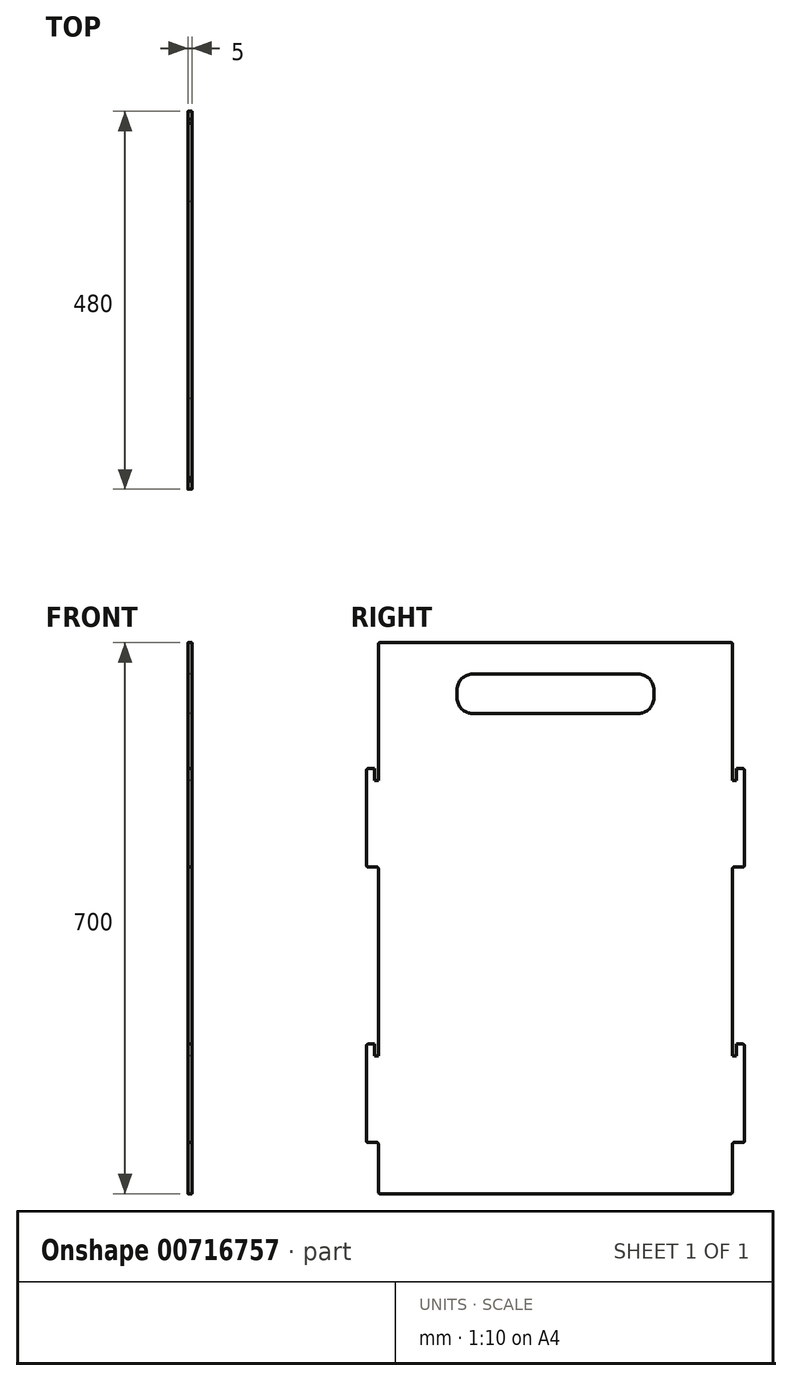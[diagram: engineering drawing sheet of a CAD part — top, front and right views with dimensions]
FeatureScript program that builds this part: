
annotation { "Feature Type Name" : "Feature", "Feature Type Description" : "" }
export const myFeature = defineFeature(function(context is Context, id is Id, definition is map)
    precondition{}
    {
        {
            var Q0;
            Q0=qCreatedBy(makeId("Right.planeOp"),FACE);
            var sketch = newSketch(context, id + "F0", { "sketchPlane" : qUnion([Q0])});
            skLineSegment(sketch, "E0.bottom", {"start": v(2, 0) * mm, "end": v(448, 0) * mm});
            skLineSegment(sketch, "E0.top", {"start": v(2, 700) * mm, "end": v(448, 700) * mm});
            skLineSegment(sketch, "E0.left", {"start": v(0, 2) * mm, "end": v(0, 63) * mm});
            skLineSegment(sketch, "E0.right", {"start": v(450, 2) * mm, "end": v(450, 63) * mm});
            skLineSegment(sketch, "E1.bottom", {"start": v(330, 610) * mm, "end": v(120, 610) * mm});
            skLineSegment(sketch, "E1.top", {"start": v(330, 660) * mm, "end": v(120, 660) * mm});
            skLineSegment(sketch, "E1.left", {"start": v(350, 630) * mm, "end": v(350, 640) * mm});
            skLineSegment(sketch, "E1.right", {"start": v(100, 630) * mm, "end": v(100, 640) * mm});
            skPoint(sketch, "E1.middle", {"position": v(225, 635) * mm});
            skPoint(sketch, "E2.visualSharp", {"position": v(100, 660) * mm});
            skArc(sketch, "E2.filletArc", {"start": v(120, 660) * mm, "mid": v(105.86, 654.14) * mm, "end": v(100, 640) * mm});
            skPoint(sketch, "E3.visualSharp", {"position": v(100, 610) * mm});
            skArc(sketch, "E3.filletArc", {"start": v(100, 630) * mm, "mid": v(105.86, 615.86) * mm, "end": v(120, 610) * mm});
            skPoint(sketch, "E4.visualSharp", {"position": v(350, 660) * mm});
            skArc(sketch, "E4.filletArc", {"start": v(350, 640) * mm, "mid": v(344.14, 654.14) * mm, "end": v(330, 660) * mm});
            skPoint(sketch, "E5.visualSharp", {"position": v(350, 610) * mm});
            skArc(sketch, "E5.filletArc", {"start": v(330, 610) * mm, "mid": v(344.14, 615.86) * mm, "end": v(350, 630) * mm});
            skLineSegment(sketch, "E6.bottom", {"start": v(-5, 540) * mm, "end": v(-13, 540) * mm});
            skLineSegment(sketch, "E6.top", {"start": v(-2, 415) * mm, "end": v(-13, 415) * mm});
            skLineSegment(sketch, "E6.right", {"start": v(-15, 538) * mm, "end": v(-15, 417) * mm});
            skLineSegment(sketch, "E7.bottom", {"start": v(-5, 190) * mm, "end": v(-13, 190) * mm});
            skLineSegment(sketch, "E7.top", {"start": v(-2, 65) * mm, "end": v(-13, 65) * mm});
            skLineSegment(sketch, "E7.right", {"start": v(-15, 188) * mm, "end": v(-15, 67) * mm});
            skLineSegment(sketch, "E8.trimOffspring", {"start": v(0, 525) * mm, "end": v(0, 698) * mm});
            skLineSegment(sketch, "E9.trimOffspring", {"start": v(0, 190) * mm, "end": v(0, 413) * mm});
            skLineSegment(sketch, "E10", {"start": v(225, 700) * mm, "end": v(225, 0) * mm, "construction": true});
            skLineSegment(sketch, "E11.MirrorCS", {"start": v(452, 65) * mm, "end": v(463, 65) * mm});
            skLineSegment(sketch, "E12.MirrorCS", {"start": v(465, 188) * mm, "end": v(465, 67) * mm});
            skLineSegment(sketch, "E13.MirrorCS", {"start": v(455, 190) * mm, "end": v(463, 190) * mm});
            skLineSegment(sketch, "E14.MirrorCS", {"start": v(452, 415) * mm, "end": v(463, 415) * mm});
            skLineSegment(sketch, "E15.MirrorCS", {"start": v(455, 540) * mm, "end": v(463, 540) * mm});
            skLineSegment(sketch, "E16.MirrorCS", {"start": v(465, 538) * mm, "end": v(465, 417) * mm});
            skLineSegment(sketch, "E17.trimOffspring", {"start": v(450, 540) * mm, "end": v(450, 698) * mm});
            skLineSegment(sketch, "E18.trimOffspring", {"start": v(450, 190) * mm, "end": v(450, 413) * mm});
            skLineSegment(sketch, "E19.top", {"start": v(-5, 525) * mm, "end": v(0, 525) * mm});
            skLineSegment(sketch, "E19.left", {"start": v(-5, 540) * mm, "end": v(-5, 525) * mm});
            skLineSegment(sketch, "E20.top", {"start": v(-5, 175) * mm, "end": v(0, 175) * mm});
            skLineSegment(sketch, "E20.left", {"start": v(-5, 190) * mm, "end": v(-5, 175) * mm});
            skLineSegment(sketch, "E20.right", {"start": v(0, 200) * mm, "end": v(0, 175) * mm});
            skLineSegment(sketch, "E21.MirrorCS", {"start": v(455, 525) * mm, "end": v(450, 525) * mm});
            skLineSegment(sketch, "E22.MirrorCS", {"start": v(455, 540) * mm, "end": v(455, 525) * mm});
            skLineSegment(sketch, "E23.MirrorCS", {"start": v(455, 190) * mm, "end": v(455, 175) * mm});
            skLineSegment(sketch, "E24.MirrorCS", {"start": v(455, 175) * mm, "end": v(450, 175) * mm});
            skLineSegment(sketch, "E25", {"start": v(450, 540) * mm, "end": v(450, 525) * mm});
            skLineSegment(sketch, "E26", {"start": v(450, 190) * mm, "end": v(450, 175) * mm});
            skPoint(sketch, "E27.orphan", {"position": v(0, 540) * mm});
            skPoint(sketch, "E28.visualSharp", {"position": v(0, 700) * mm});
            skArc(sketch, "E28.filletArc", {"start": v(2, 700) * mm, "mid": v(0.59, 699.41) * mm, "end": v(0, 698) * mm});
            skPoint(sketch, "E29.visualSharp", {"position": v(450, 700) * mm});
            skArc(sketch, "E29.filletArc", {"start": v(450, 698) * mm, "mid": v(449.41, 699.41) * mm, "end": v(448, 700) * mm});
            skPoint(sketch, "E30.visualSharp", {"position": v(-15, 540) * mm});
            skArc(sketch, "E30.filletArc", {"start": v(-13, 540) * mm, "mid": v(-14.41, 539.41) * mm, "end": v(-15, 538) * mm});
            skPoint(sketch, "E31.visualSharp", {"position": v(-15, 415) * mm});
            skArc(sketch, "E31.filletArc", {"start": v(-15, 417) * mm, "mid": v(-14.41, 415.59) * mm, "end": v(-13, 415) * mm});
            skPoint(sketch, "E32.visualSharp", {"position": v(0, 415) * mm});
            skArc(sketch, "E32.filletArc", {"start": v(0, 413) * mm, "mid": v(-0.59, 414.41) * mm, "end": v(-2, 415) * mm});
            skPoint(sketch, "E33.visualSharp", {"position": v(-15, 190) * mm});
            skArc(sketch, "E33.filletArc", {"start": v(-13, 190) * mm, "mid": v(-14.41, 189.41) * mm, "end": v(-15, 188) * mm});
            skPoint(sketch, "E34.visualSharp", {"position": v(-15, 65) * mm});
            skArc(sketch, "E34.filletArc", {"start": v(-15, 67) * mm, "mid": v(-14.41, 65.59) * mm, "end": v(-13, 65) * mm});
            skPoint(sketch, "E35.visualSharp", {"position": v(0, 65) * mm});
            skArc(sketch, "E35.filletArc", {"start": v(0, 63) * mm, "mid": v(-0.59, 64.41) * mm, "end": v(-2, 65) * mm});
            skPoint(sketch, "E36.visualSharp", {"position": v(0, 0) * mm});
            skArc(sketch, "E36.filletArc", {"start": v(0, 2) * mm, "mid": v(0.59, 0.59) * mm, "end": v(2, 0) * mm});
            skPoint(sketch, "E37.visualSharp", {"position": v(450, 0) * mm});
            skArc(sketch, "E37.filletArc", {"start": v(448, 0) * mm, "mid": v(449.41, 0.59) * mm, "end": v(450, 2) * mm});
            skPoint(sketch, "E38.visualSharp", {"position": v(450, 65) * mm});
            skArc(sketch, "E38.filletArc", {"start": v(452, 65) * mm, "mid": v(450.59, 64.41) * mm, "end": v(450, 63) * mm});
            skPoint(sketch, "E39.visualSharp", {"position": v(465, 65) * mm});
            skArc(sketch, "E39.filletArc", {"start": v(463, 65) * mm, "mid": v(464.41, 65.59) * mm, "end": v(465, 67) * mm});
            skPoint(sketch, "E40.visualSharp", {"position": v(465, 190) * mm});
            skArc(sketch, "E40.filletArc", {"start": v(465, 188) * mm, "mid": v(464.41, 189.41) * mm, "end": v(463, 190) * mm});
            skPoint(sketch, "E41.visualSharp", {"position": v(450, 415) * mm});
            skArc(sketch, "E41.filletArc", {"start": v(452, 415) * mm, "mid": v(450.59, 414.41) * mm, "end": v(450, 413) * mm});
            skPoint(sketch, "E42.visualSharp", {"position": v(465, 415) * mm});
            skArc(sketch, "E42.filletArc", {"start": v(463, 415) * mm, "mid": v(464.41, 415.59) * mm, "end": v(465, 417) * mm});
            skPoint(sketch, "E43.visualSharp", {"position": v(465, 540) * mm});
            skArc(sketch, "E43.filletArc", {"start": v(465, 538) * mm, "mid": v(464.41, 539.41) * mm, "end": v(463, 540) * mm});
            skSolve(sketch);
        }
        {
            var Q0;
            Q0=makeQuery(id+"F0.imprint","IMPRINT",FACE,{"disambiguationData":[TD([[makeQuery(id+"F0.imprint","IMPRINT",EDGE,{"derivedFrom":sQuery(id+"F0.wireOp",EDGE,"E0.bottom")}),1.0]])]});
            extrude(context, id + "F1", {"entities" : qUnion([Q0]), "depth" : 5 * mm, "offsetDistance" : 25 * mm});
        }
    });
